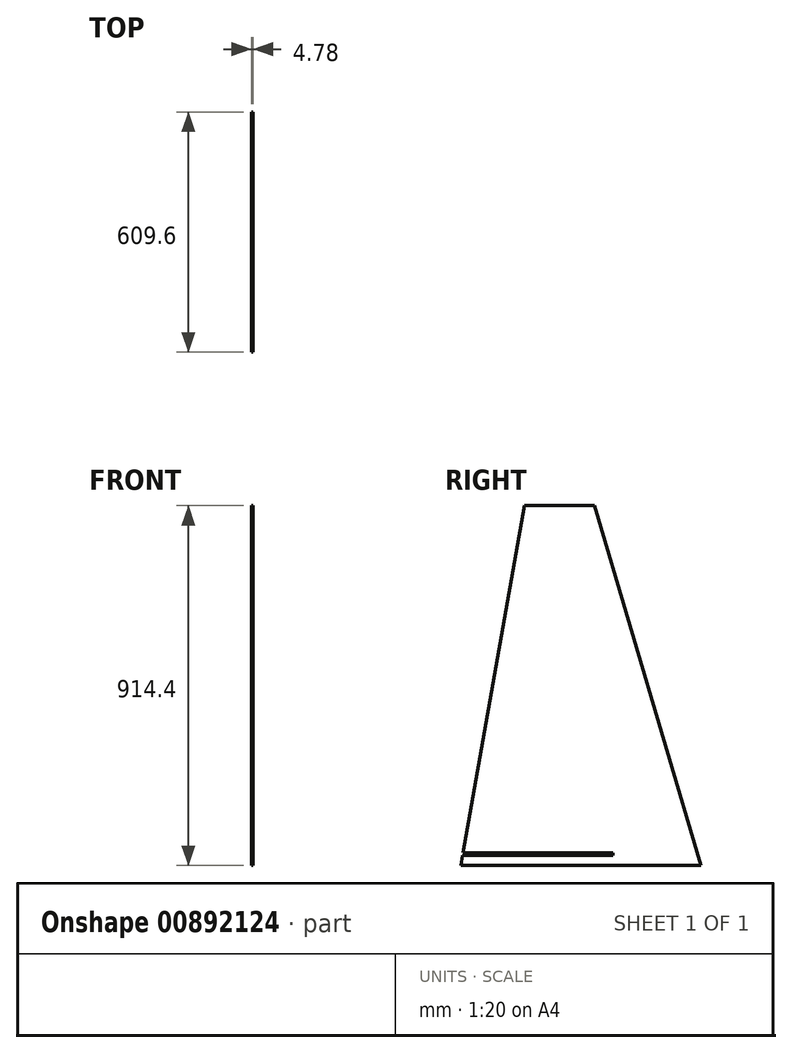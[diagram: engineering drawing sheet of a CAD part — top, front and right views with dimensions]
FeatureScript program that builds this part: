
annotation { "Feature Type Name" : "Feature", "Feature Type Description" : "" }
export const myFeature = defineFeature(function(context is Context, id is Id, definition is map)
    precondition{}
    {
        {
            var Q0;
            Q0=qCreatedBy(makeId("Right.planeOp"),FACE);
            var sketch = newSketch(context, id + "F0", { "sketchPlane" : qUnion([Q0])});
            skLineSegment(sketch, "E0", {"start": v(-114.17, 609.23) * mm, "end": v(63.63, 609.23) * mm});
            skLineSegment(sketch, "E1", {"start": v(63.63, 609.23) * mm, "end": v(334.2, -305.17) * mm});
            skLineSegment(sketch, "E2", {"start": v(334.2, -305.17) * mm, "end": v(-275.4, -305.17) * mm});
            skLineSegment(sketch, "E3", {"start": v(-275.4, -305.17) * mm, "end": v(-114.17, 609.23) * mm});
            skSolve(sketch);
        }
        {
            var Q0;
            Q0=makeQuery(id+"F0.imprint","IMPRINT",FACE,{"disambiguationData":[TD([[makeQuery(id+"F0.imprint","IMPRINT",EDGE,{"derivedFrom":sQuery(id+"F0.wireOp",EDGE,"E0")}),-1.0]])]});
            extrude(context, id + "F1", {"entities" : qUnion([Q0]), "depth" : 4.78 * mm, "offsetDistance" : 25.4 * mm});
        }
        {
            var Q0;
            Q0=makeQuery(id+"F1.opExtrude","CAP_FACE",FACE,{"disambiguationData":[OSD([sQuery(id+"F0.wireOp",EDGE,"E0"),sQuery(id+"F0.wireOp",EDGE,"E1"),sQuery(id+"F0.wireOp",EDGE,"E2"),sQuery(id+"F0.wireOp",EDGE,"E3")])],"isStart":false});
            var sketch = newSketch(context, id + "F2", { "sketchPlane" : qUnion([Q0])});
            skLineSegment(sketch, "E4", {"start": v(-269.8, -273.42) * mm, "end": v(111.2, -273.42) * mm});
            skLineSegment(sketch, "E5", {"start": v(111.2, -273.42) * mm, "end": v(111.2, -279.77) * mm});
            skLineSegment(sketch, "E6", {"start": v(111.2, -279.77) * mm, "end": v(-327.72, -279.77) * mm});
            skLineSegment(sketch, "E7", {"start": v(-327.72, -279.77) * mm, "end": v(-327.72, -273.42) * mm});
            skLineSegment(sketch, "E8", {"start": v(-327.72, -273.42) * mm, "end": v(-269.8, -273.42) * mm});
            skSolve(sketch);
        }
        {
            var Q0;
            Q0 = qSketchRegion(id + "F2", true);
            extrude(context, id + "F3", {"entities" : qUnion([Q0]), "operationType" : NewBodyOperationType.REMOVE, "oppositeDirection" : true, "depth" : 25.4 * mm, "offsetDistance" : 25.4 * mm});
        }
    });
